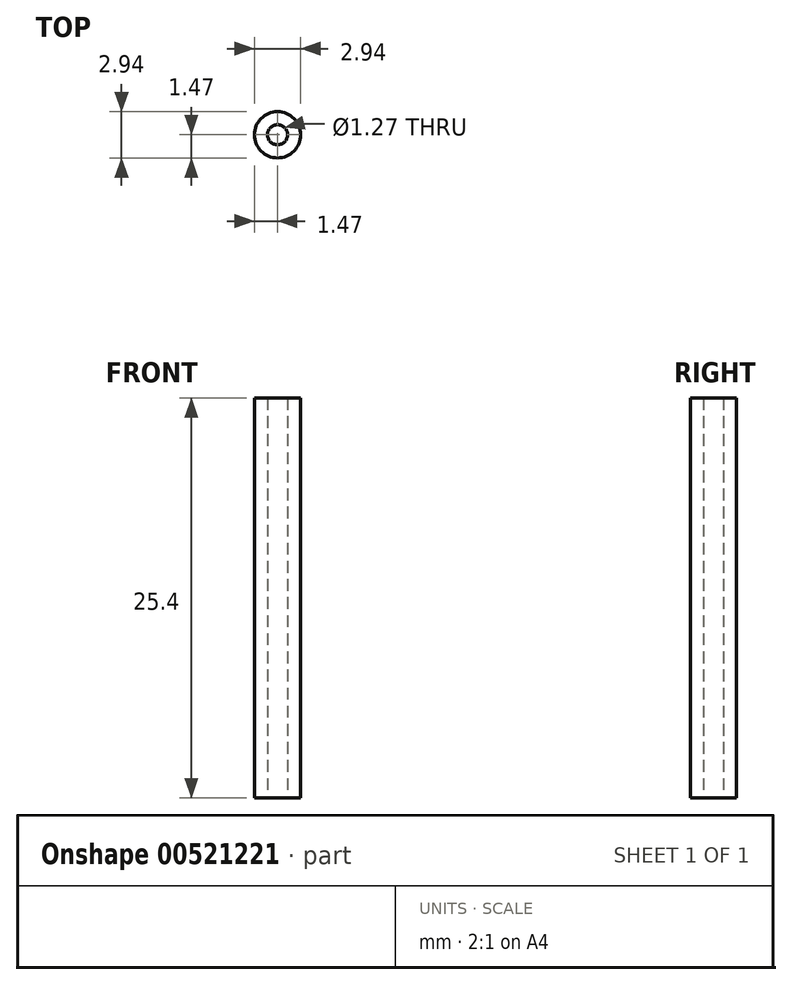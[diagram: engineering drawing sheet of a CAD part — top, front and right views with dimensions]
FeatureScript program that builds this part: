
annotation { "Feature Type Name" : "Feature", "Feature Type Description" : "" }
export const myFeature = defineFeature(function(context is Context, id is Id, definition is map)
    precondition{}
    {
        {
            var Q0;
            Q0=qCreatedBy(makeId("Top.planeOp"),FACE);
            var sketch = newSketch(context, id + "F0", { "sketchPlane" : qUnion([Q0])});
            skCircle(sketch, "E0", {"center": v(0, 0) * mm, "radius": 1.47 * mm});
            skCircle(sketch, "E1", {"center": v(0, 0) * mm, "radius": 0.64 * mm});
            skSolve(sketch);
        }
        {
            var Q0;
            Q0=makeQuery(id+"F0.imprint","IMPRINT",FACE,{"disambiguationData":[TD([[makeQuery(id+"F0.imprint","IMPRINT",EDGE,{"derivedFrom":sQuery(id+"F0.wireOp",EDGE,"E0")}),1.0]])]});
            extrude(context, id + "F1", {"entities" : qUnion([Q0]), "depth" : 25.4 * mm, "offsetDistance" : 25.4 * mm});
        }
    });
